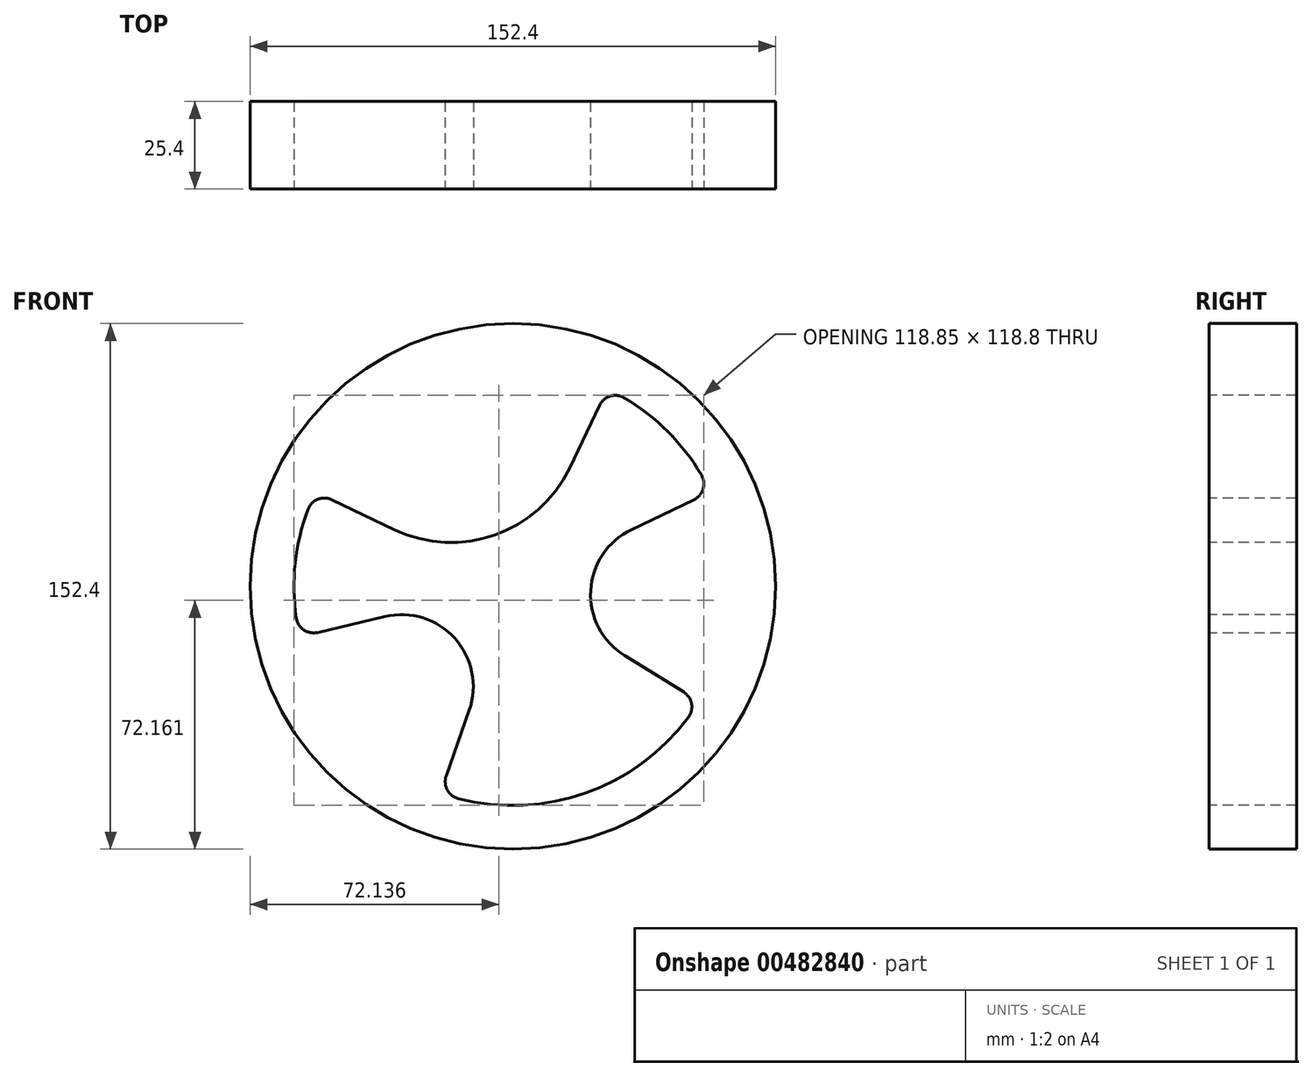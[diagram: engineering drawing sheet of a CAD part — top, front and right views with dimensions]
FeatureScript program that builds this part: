
annotation { "Feature Type Name" : "Feature", "Feature Type Description" : "" }
export const myFeature = defineFeature(function(context is Context, id is Id, definition is map)
    precondition{}
    {
        {
            var Q0;
            Q0=qCreatedBy(makeId("Front.planeOp"),FACE);
            var sketch = newSketch(context, id + "F0", { "sketchPlane" : qUnion([Q0])});
            skCircle(sketch, "E0", {"center": v(0, 0) * mm, "radius": 76.2 * mm});
            skSolve(sketch);
        }
        {
            var Q0;
            Q0=makeQuery(id+"F0.imprint","IMPRINT",FACE,{"disambiguationData":[TD([[makeQuery(id+"F0.imprint","IMPRINT",EDGE,{"derivedFrom":sQuery(id+"F0.wireOp",EDGE,"E0")}),1.0]])]});
            extrude(context, id + "F1", {"entities" : qUnion([Q0]), "depth" : 25.4 * mm});
        }
        {
            var Q0;
            Q0=makeQuery(id+"F1.opExtrude","CAP_FACE",FACE,{"disambiguationData":[OSD([sQuery(id+"F0.wireOp",EDGE,"E0")])],"isStart":false});
            var sketch = newSketch(context, id + "F2", { "sketchPlane" : qUnion([Q0])});
            skPoint(sketch, "E1.center.orphan", {"position": v(0, 50.8) * mm});
            skLineSegment(sketch, "E2.1.0", {"start": v(-34.37, 16.45) * mm, "end": v(-52.5, 25.13) * mm});
            skLineSegment(sketch, "E2.4.2", {"start": v(-12.67, -35.93) * mm, "end": v(-19.35, -54.89) * mm});
            skLineSegment(sketch, "E2.7.0", {"start": v(16.45, 34.37) * mm, "end": v(25.13, 52.5) * mm});
            skLineSegment(sketch, "E2.7.2", {"start": v(34.37, 16.45) * mm, "end": v(52.5, 25.13) * mm});
            skPoint(sketch, "E2.center", {"position": v(0, 0) * mm});
            skLineSegment(sketch, "E3", {"start": v(-37.08, -8.74) * mm, "end": v(-56.65, -13.35) * mm});
            skPoint(sketch, "E4.orphan", {"position": v(-63.84, -22.5) * mm});
            skPoint(sketch, "E5.center.orphan", {"position": v(-50.5, 5.45) * mm});
            skPoint(sketch, "E6.orphan", {"position": v(-63.84, 22.5) * mm});
            skPoint(sketch, "E7.orphan", {"position": v(-23.95, 8.45) * mm});
            skPoint(sketch, "E8.orphan", {"position": v(-23.95, -8.45) * mm});
            skLineSegment(sketch, "E9", {"start": v(32.4, -20.04) * mm, "end": v(49.5, -30.61) * mm});
            skPoint(sketch, "E10.orphan", {"position": v(22.91, -10.97) * mm});
            skPoint(sketch, "E11.orphan", {"position": v(61.06, -29.23) * mm});
            skPoint(sketch, "E12.center.orphan", {"position": v(31.86, -39.57) * mm});
            skPoint(sketch, "E13.orphan", {"position": v(8.45, -23.95) * mm});
            skPoint(sketch, "E14.orphan", {"position": v(22.5, -63.84) * mm});
            skArc(sketch, "E15", {"start": v(-59.44, 22.33) * mm, "mid": v(-63.13, 6.81) * mm, "end": v(-62.84, -9.14) * mm});
            skPoint(sketch, "E16.orphan", {"position": v(61.06, 29.23) * mm});
            skArc(sketch, "E17.trimOffspring", {"start": v(-15.83, -61.5) * mm, "mid": v(21.11, -59.89) * mm, "end": v(50.9, -37.97) * mm});
            skPoint(sketch, "E18.orphan", {"position": v(-61.06, 29.23) * mm});
            skPoint(sketch, "E19.orphan", {"position": v(-22.5, -63.84) * mm});
            skArc(sketch, "E20.trimOffspring", {"start": v(54.68, 32.3) * mm, "mid": v(44.9, 44.9) * mm, "end": v(32.3, 54.68) * mm});
            skPoint(sketch, "E21.orphan", {"position": v(22.91, 10.97) * mm});
            skArc(sketch, "E22", {"start": v(-12.67, -35.93) * mm, "mid": v(-16.81, -15.1) * mm, "end": v(-37.08, -8.74) * mm});
            skArc(sketch, "E23", {"start": v(-34.37, 16.45) * mm, "mid": v(-5.25, 14.88) * mm, "end": v(16.45, 34.37) * mm});
            skArc(sketch, "E24", {"start": v(34.37, 16.45) * mm, "mid": v(22.56, -1.21) * mm, "end": v(32.4, -20.04) * mm});
            skPoint(sketch, "E25.visualSharp", {"position": v(-57.28, 27.42) * mm});
            skArc(sketch, "E25.filletArc", {"start": v(-52.5, 25.13) * mm, "mid": v(-56.58, 25.26) * mm, "end": v(-59.44, 22.33) * mm});
            skPoint(sketch, "E26.visualSharp", {"position": v(-61.8, -14.57) * mm});
            skArc(sketch, "E26.filletArc", {"start": v(-62.84, -9.14) * mm, "mid": v(-60.67, -12.6) * mm, "end": v(-56.65, -13.35) * mm});
            skPoint(sketch, "E27.visualSharp", {"position": v(-21.11, -59.89) * mm});
            skArc(sketch, "E27.filletArc", {"start": v(-19.35, -54.89) * mm, "mid": v(-19.04, -58.97) * mm, "end": v(-15.83, -61.5) * mm});
            skPoint(sketch, "E28.visualSharp", {"position": v(54, -33.4) * mm});
            skArc(sketch, "E28.filletArc", {"start": v(50.9, -37.97) * mm, "mid": v(51.81, -33.99) * mm, "end": v(49.5, -30.61) * mm});
            skPoint(sketch, "E29.visualSharp", {"position": v(57.28, 27.42) * mm});
            skArc(sketch, "E29.filletArc", {"start": v(52.5, 25.13) * mm, "mid": v(55.16, 28.23) * mm, "end": v(54.68, 32.3) * mm});
            skPoint(sketch, "E30.visualSharp", {"position": v(27.42, 57.28) * mm});
            skArc(sketch, "E30.filletArc", {"start": v(32.3, 54.68) * mm, "mid": v(28.23, 55.16) * mm, "end": v(25.13, 52.5) * mm});
            skSolve(sketch);
        }
        {
            var Q0;
            Q0 = qSketchRegion(id + "F2", true);
            extrude(context, id + "F3", {"entities" : qUnion([Q0]), "operationType" : NewBodyOperationType.REMOVE, "oppositeDirection" : true, "depth" : 25.4 * mm});
        }
    });
